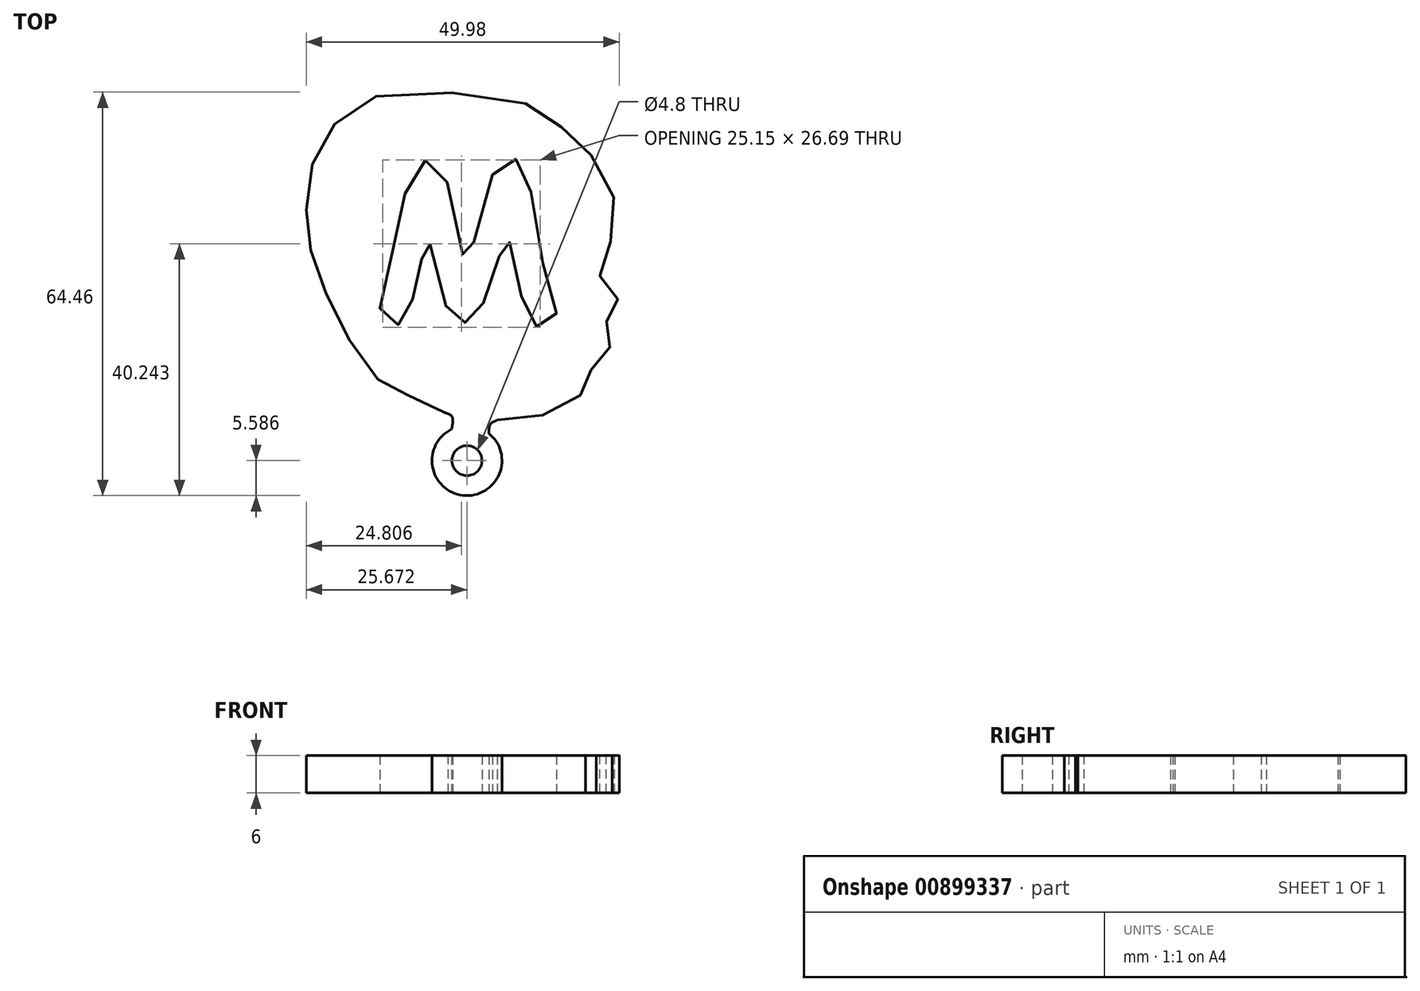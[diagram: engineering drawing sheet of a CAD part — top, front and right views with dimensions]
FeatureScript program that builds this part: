
annotation { "Feature Type Name" : "Feature", "Feature Type Description" : "" }
export const myFeature = defineFeature(function(context is Context, id is Id, definition is map)
    precondition{}
    {
        {
            var Q0;
            Q0=qCreatedBy(makeId("Top.planeOp"),FACE);
            var sketch = newSketch(context, id + "F0", { "sketchPlane" : qUnion([Q0])});
            skCircle(sketch, "E0", {"center": v(-3.5, -54.6) * mm, "radius": 2.4 * mm});
            skCircle(sketch, "E1", {"center": v(-3.5, -54.6) * mm, "radius": 5.59 * mm});
            skLineSegment(sketch, "E2", {"start": v(-3.2, -52.22) * mm, "end": v(-3.2, -49.02) * mm, "construction": true});
            skFitSpline(sketch, "E3", {"points": [v(19.33, -20.03) * mm, v(18.58, -21.94) * mm, v(17.84, -24.16) * mm, v(17.8, -25.55) * mm, v(18.23, -26.65) * mm, v(18.95, -27.42) * mm, v(20.41, -28.63) * mm, v(20.8, -29.69) * mm, v(20.4, -30.98) * mm, v(19.02, -32.1) * mm, v(18.8, -32.36) * mm, v(18.78, -32.81) * mm, v(19.64, -35.14) * mm, v(19.69, -35.52) * mm, v(19.58, -36.06) * mm, v(18.88, -36.92) * mm, v(17.14, -38.12) * mm, v(17.13, -38.37) * mm, v(16.89, -39.62) * mm, v(15.47, -40.51) * mm, v(15.35, -40.6) * mm, v(15.45, -41.52) * mm, v(15.02, -43.5) * mm, v(13.12, -45.6) * mm, v(10.67, -46.55) * mm, v(7.27, -47.75) * mm, v(3.47, -48.1) * mm, v(1.43, -48.1) * mm, v(0.08, -48.54) * mm, v(-7.25, -46.85) * mm, v(-8.17, -46.4) * mm, v(-10.57, -45.07) * mm, v(-13.29, -44.07) * mm, v(-14.49, -43.75) * mm, v(-16.2, -43) * mm, v(-18.23, -41) * mm, v(-21.27, -37.12) * mm, v(-22.18, -35.48) * mm, v(-24.57, -29.95) * mm, v(-25.85, -28.05) * mm, v(-26.7, -26.76) * mm, v(-28.1, -22.51) * mm, v(-28.69, -19.46) * mm, v(-29.07, -16.74) * mm, v(-29.16, -14.57) * mm, v(-28.9, -10.61) * mm, v(-28.34, -7.74) * mm, v(-27.52, -5.55) * mm, v(-25.69, -2.36) * mm, v(-23.37, 0.57) * mm, v(-19.8, 2.97) * mm, v(-15.93, 3.98) * mm, v(-4.9, 4.12) * mm, v(4.72, 2.8) * mm, v(7.1, 1.9) * mm, v(9.77, 0.34) * mm, v(12.02, -1.74) * mm, v(13.91, -3.4) * mm, v(15.43, -4.74) * mm, v(18.42, -8.8) * mm, v(19.65, -11.21) * mm, v(20.06, -13.88) * mm, v(19.96, -16.87) * mm, v(19.33, -20.03) * mm]});
            skFitSpline(sketch, "E4", {"points": [v(1.43, -48.1) * mm, v(0.26, -48.74) * mm, v(0, -50.25) * mm], "startDerivative": vector(-2.88, -0.97) * mm, "endDerivative": vector(-0.01, -3.31) * mm});
            skFitSpline(sketch, "E5", {"points": [v(-7.25, -46.85) * mm, v(-5.9, -47.58) * mm, v(-5.95, -49.58) * mm], "startDerivative": vector(3.57, -1.04) * mm, "endDerivative": vector(-0.86, -4.34) * mm});
            skFitSpline(sketch, "E6", {"points": [v(6.73, -11.7) * mm, v(7.99, -20.06) * mm, v(9.7, -26.93) * mm, v(10.73, -30.51) * mm, v(10.75, -31.6) * mm, v(10.3, -32.43) * mm, v(9.18, -33.18) * mm, v(7.64, -33.17) * mm, v(6.5, -32.27) * mm, v(5.8, -30.85) * mm, v(5.19, -28.31) * mm, v(3.97, -23.13) * mm, v(3.22, -18.98) * mm, v(3.1, -18.03) * mm, v(3.04, -18.2) * mm, v(1.9, -21.28) * mm, v(0.58, -25.17) * mm, v(-0.7, -29) * mm, v(-1.8, -31.35) * mm, v(-2.37, -31.94) * mm, v(-2.93, -32.37) * mm, v(-3.94, -32.58) * mm, v(-4.67, -32.58) * mm, v(-5.62, -32.1) * mm, v(-6.5, -30.78) * mm, v(-7.26, -28.4) * mm, v(-9.28, -20.6) * mm, v(-9.74, -18.91) * mm, v(-9.79, -18.86) * mm, v(-9.97, -19.31) * mm, v(-10.54, -21.6) * mm, v(-11.42, -24.98) * mm, v(-11.88, -27.08) * mm, v(-12.38, -29.94) * mm, v(-12.78, -31.52) * mm, v(-13.62, -32.54) * mm, v(-14.63, -32.93) * mm, v(-15.87, -32.83) * mm, v(-16.75, -32.2) * mm, v(-17.31, -31.17) * mm, v(-17.04, -27.53) * mm, v(-15.33, -20.95) * mm, v(-14.42, -17.76) * mm, v(-13.17, -11.09) * mm, v(-11.92, -7.8) * mm, v(-10.62, -6.77) * mm, v(-9.43, -6.6) * mm, v(-8.27, -6.8) * mm, v(-7.06, -8.68) * mm, v(-5.85, -14.61) * mm, v(-3.93, -22.76) * mm, v(-3.77, -23.28) * mm, v(-3.71, -23.3) * mm, v(-3.48, -22.53) * mm, v(-1.66, -17.54) * mm, v(0.45, -9.37) * mm, v(1.23, -7.59) * mm, v(2.63, -6.45) * mm, v(3.9, -6.35) * mm, v(5.36, -7.29) * mm, v(6.35, -9.96) * mm, v(6.73, -11.7) * mm]});
            skSolve(sketch);
        }
        {
            var Q0;
            {var subQ0=sQuery(id+"F0.wireOp",EDGE,"E4");var subQ1=sQuery(id+"F0.wireOp",EDGE,"E3");var subQ2=makeQuery(id+"F0.imprint","INTERSECT",VERTEX,{"disambiguationData":[OD(0.0)],"derivedFrom":[subQ1,subQ0]});Q0=makeQuery(id+"F0.imprint","IMPRINT",FACE,{"disambiguationData":[TD([[makeQuery(id+"F0.imprint","IMPRINT",EDGE,{"disambiguationData":[TD([[subQ2,-1.0]])],"derivedFrom":subQ1}),1.0]])]});}
            var Q1;
            {var subQ0=sQuery(id+"F0.wireOp",EDGE,"E4");var subQ1=sQuery(id+"F0.wireOp",EDGE,"E3");var subQ2=makeQuery(id+"F0.imprint","INTERSECT",VERTEX,{"disambiguationData":[OD(1.0)],"derivedFrom":[subQ1,subQ0]});Q1=makeQuery(id+"F0.imprint","IMPRINT",FACE,{"disambiguationData":[TD([[makeQuery(id+"F0.imprint","IMPRINT",EDGE,{"disambiguationData":[TD([[subQ2,-1.0]])],"derivedFrom":subQ1}),-1.0]])]});}
            var Q2;
            {var subQ0=sQuery(id+"F0.wireOp",EDGE,"E5");var subQ1=sQuery(id+"F0.wireOp",EDGE,"E3");var subQ2=makeQuery(id+"F0.imprint","INTERSECT",VERTEX,{"disambiguationData":[OD(0.0)],"derivedFrom":[subQ1,subQ0]});Q2=makeQuery(id+"F0.imprint","IMPRINT",FACE,{"disambiguationData":[TD([[makeQuery(id+"F0.imprint","IMPRINT",EDGE,{"disambiguationData":[TD([[subQ2,1.0]])],"derivedFrom":subQ1}),-1.0]])]});}
            var Q3;
            Q3=makeQuery(id+"F0.imprint","IMPRINT",FACE,{"disambiguationData":[TD([[makeQuery(id+"F0.imprint","IMPRINT",EDGE,{"derivedFrom":sQuery(id+"F0.wireOp",EDGE,"E0")}),-1.0]])]});
            var Q4;
            {var subQ0=sQuery(id+"F0.wireOp",EDGE,"E4");var subQ1=sQuery(id+"F0.wireOp",EDGE,"E1");var subQ2=makeQuery(id+"F0.imprint","INTERSECT",VERTEX,{"derivedFrom":[subQ1,subQ0]});Q4=makeQuery(id+"F0.imprint","IMPRINT",FACE,{"disambiguationData":[TD([[makeQuery(id+"F0.imprint","IMPRINT",EDGE,{"disambiguationData":[TD([[subQ2,-1.0]])],"derivedFrom":subQ1}),-1.0]])]});}
            extrude(context, id + "F1", {"entities" : qUnion([Q0, Q1, Q2, Q3, Q4]), "depth" : 6 * mm, "offsetDistance" : 25 * mm});
        }
        {
            var Q0;
            Q0 = qSketchRegion(id + "F0", true);
            extrude(context, id + "F2", {"entities" : qUnion([Q0]), "operationType" : NewBodyOperationType.ADD, "depth" : 6 * mm, "offsetDistance" : 25 * mm});
        }
    });
